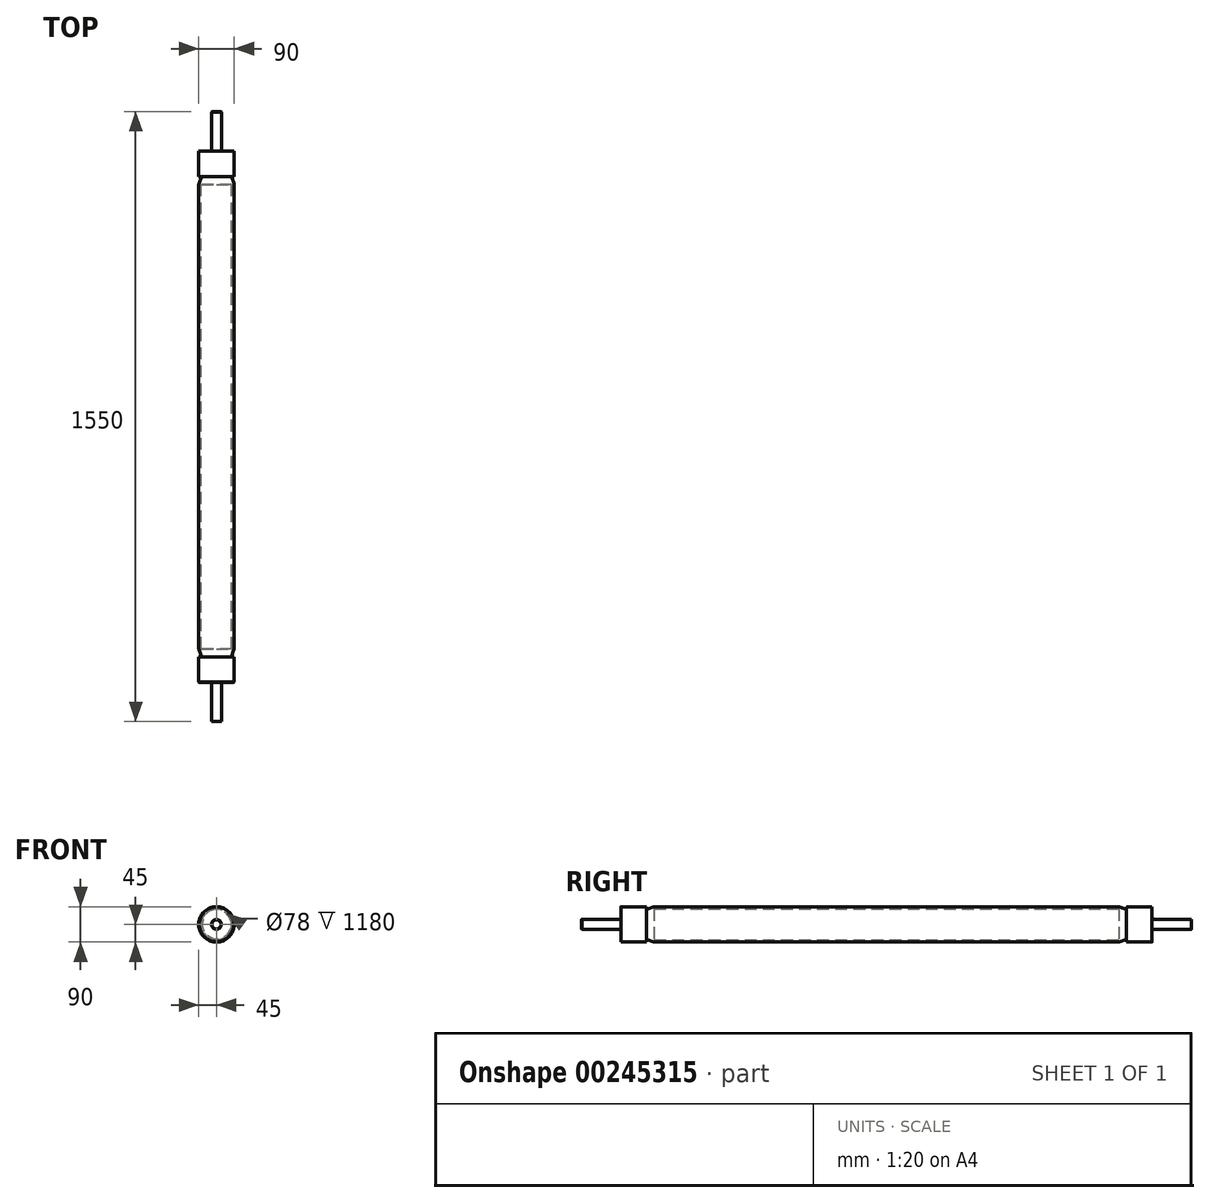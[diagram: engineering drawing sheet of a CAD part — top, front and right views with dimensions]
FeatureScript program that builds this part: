
annotation { "Feature Type Name" : "Feature", "Feature Type Description" : "" }
export const myFeature = defineFeature(function(context is Context, id is Id, definition is map)
    precondition{}
    {
        {
            var Q0;
            Q0=qCreatedBy(makeId("Right.planeOp"),FACE);
            var sketch = newSketch(context, id + "F0", { "sketchPlane" : qUnion([Q0])});
            skLineSegment(sketch, "E0", {"start": v(0, 0) * mm, "end": v(0, 12.5) * mm});
            skLineSegment(sketch, "E1", {"start": v(0, 12.5) * mm, "end": v(100, 12.5) * mm});
            skLineSegment(sketch, "E2", {"start": v(100, 12.5) * mm, "end": v(100, 45) * mm});
            skLineSegment(sketch, "E3", {"start": v(165, 45) * mm, "end": v(165, 38.43) * mm});
            skLineSegment(sketch, "E4", {"start": v(187.64, 45) * mm, "end": v(1363.24, 45) * mm});
            skLineSegment(sketch, "E5", {"start": v(1385, 45) * mm, "end": v(1450, 45) * mm});
            skLineSegment(sketch, "E6", {"start": v(1450, 45) * mm, "end": v(1450, 12.5) * mm});
            skLineSegment(sketch, "E7", {"start": v(1450, 12.5) * mm, "end": v(1550, 12.5) * mm});
            skLineSegment(sketch, "E8", {"start": v(1550, 12.5) * mm, "end": v(1550, 0) * mm});
            skLineSegment(sketch, "E9", {"start": v(1550, 0) * mm, "end": v(1365, 0) * mm});
            skLineSegment(sketch, "E10", {"start": v(165, 45) * mm, "end": v(100, 45) * mm});
            skPoint(sketch, "E11.visualSharp", {"position": v(1385, 37.72) * mm});
            skLineSegment(sketch, "E12", {"start": v(185, 39) * mm, "end": v(1365, 39) * mm});
            skLineSegment(sketch, "E13", {"start": v(1365, 39) * mm, "end": v(1365, 0) * mm});
            skLineSegment(sketch, "E14", {"start": v(185, 39) * mm, "end": v(185, 0) * mm});
            skLineSegment(sketch, "E15.trimOffspring", {"start": v(185, 0) * mm, "end": v(0, 0) * mm});
            skLineSegment(sketch, "E16", {"start": v(165.67, 37.96) * mm, "end": v(182.51, 44.1) * mm});
            skLineSegment(sketch, "E17", {"start": v(1366.66, 44.4) * mm, "end": v(1384.33, 37.96) * mm});
            skLineSegment(sketch, "E18", {"start": v(1385, 38.43) * mm, "end": v(1385, 45) * mm});
            skPoint(sketch, "E19.visualSharp", {"position": v(185, 45) * mm});
            skArc(sketch, "E19.filletArc", {"start": v(187.64, 45) * mm, "mid": v(185.04, 44.77) * mm, "end": v(182.51, 44.1) * mm});
            skPoint(sketch, "E20.visualSharp", {"position": v(165, 37.72) * mm});
            skArc(sketch, "E20.filletArc", {"start": v(165, 38.43) * mm, "mid": v(165.21, 38.03) * mm, "end": v(165.67, 37.96) * mm});
            skArc(sketch, "E21.filletArc", {"start": v(1384.33, 37.96) * mm, "mid": v(1384.79, 38.03) * mm, "end": v(1385, 38.43) * mm});
            skPoint(sketch, "E22.visualSharp", {"position": v(1365, 45) * mm});
            skArc(sketch, "E22.filletArc", {"start": v(1366.66, 44.4) * mm, "mid": v(1364.97, 44.85) * mm, "end": v(1363.24, 45) * mm});
            skSolve(sketch);
        }
        {
            var Q0;
            Q0=makeQuery(id+"F0.imprint","IMPRINT",FACE,{"disambiguationData":[TD([[makeQuery(id+"F0.imprint","IMPRINT",EDGE,{"derivedFrom":sQuery(id+"F0.wireOp",EDGE,"E0")}),-1.0]])]});
            var Q1;
            Q1=sQuery(id+"F0.wireOp",EDGE,"E9");
            revolve(context, id + "F1", {"surfaceOperationType" : NewSurfaceOperationType.NEW, "entities" : qUnion([Q0]), "axis" : qUnion([Q1]), "revolveType" : RevolveType.FULL});
        }
        {
            var Q0;
            Q0=makeQuery(id+"F1.opRevolve","SWEPT_EDGE",EDGE,{"disambiguationData":[OSD([sQuery(id+"F0.wireOp",EDGE,"E6"),sQuery(id+"F0.wireOp",EDGE,"E7")])]});
            var Q1;
            Q1=makeQuery(id+"F1.opRevolve","SWEPT_EDGE",EDGE,{"disambiguationData":[OSD([sQuery(id+"F0.wireOp",EDGE,"E1"),sQuery(id+"F0.wireOp",EDGE,"E2")])]});
            fillet(context, id + "F2", {"entities" : qUnion([Q0, Q1]), "tangentPropagation" : true, "radius" : 5 * mm, "defaultsChanged" : false, "vertexSettings" : [], "allowEdgeOverflow" : false});
        }
        {
            var Q0;
            Q0=makeQuery(id+"F1.opRevolve","SWEPT_EDGE",EDGE,{"disambiguationData":[OSD([sQuery(id+"F0.wireOp",EDGE,"E5"),sQuery(id+"F0.wireOp",EDGE,"E6")])]});
            var Q1;
            Q1=makeQuery(id+"F1.opRevolve","SWEPT_EDGE",EDGE,{"disambiguationData":[OSD([sQuery(id+"F0.wireOp",EDGE,"E7"),sQuery(id+"F0.wireOp",EDGE,"E8")])]});
            var Q2;
            Q2=makeQuery(id+"F1.opRevolve","SWEPT_EDGE",EDGE,{"disambiguationData":[OSD([sQuery(id+"F0.wireOp",EDGE,"E0"),sQuery(id+"F0.wireOp",EDGE,"E1")])]});
            var Q3;
            Q3=makeQuery(id+"F1.opRevolve","SWEPT_EDGE",EDGE,{"disambiguationData":[OSD([sQuery(id+"F0.wireOp",EDGE,"E2"),sQuery(id+"F0.wireOp",EDGE,"E10")])]});
            chamfer(context, id + "F3", {"entities" : qUnion([Q0, Q1, Q2, Q3]), "width" : 1 * mm, "tangentPropagation" : true});
        }
    });
